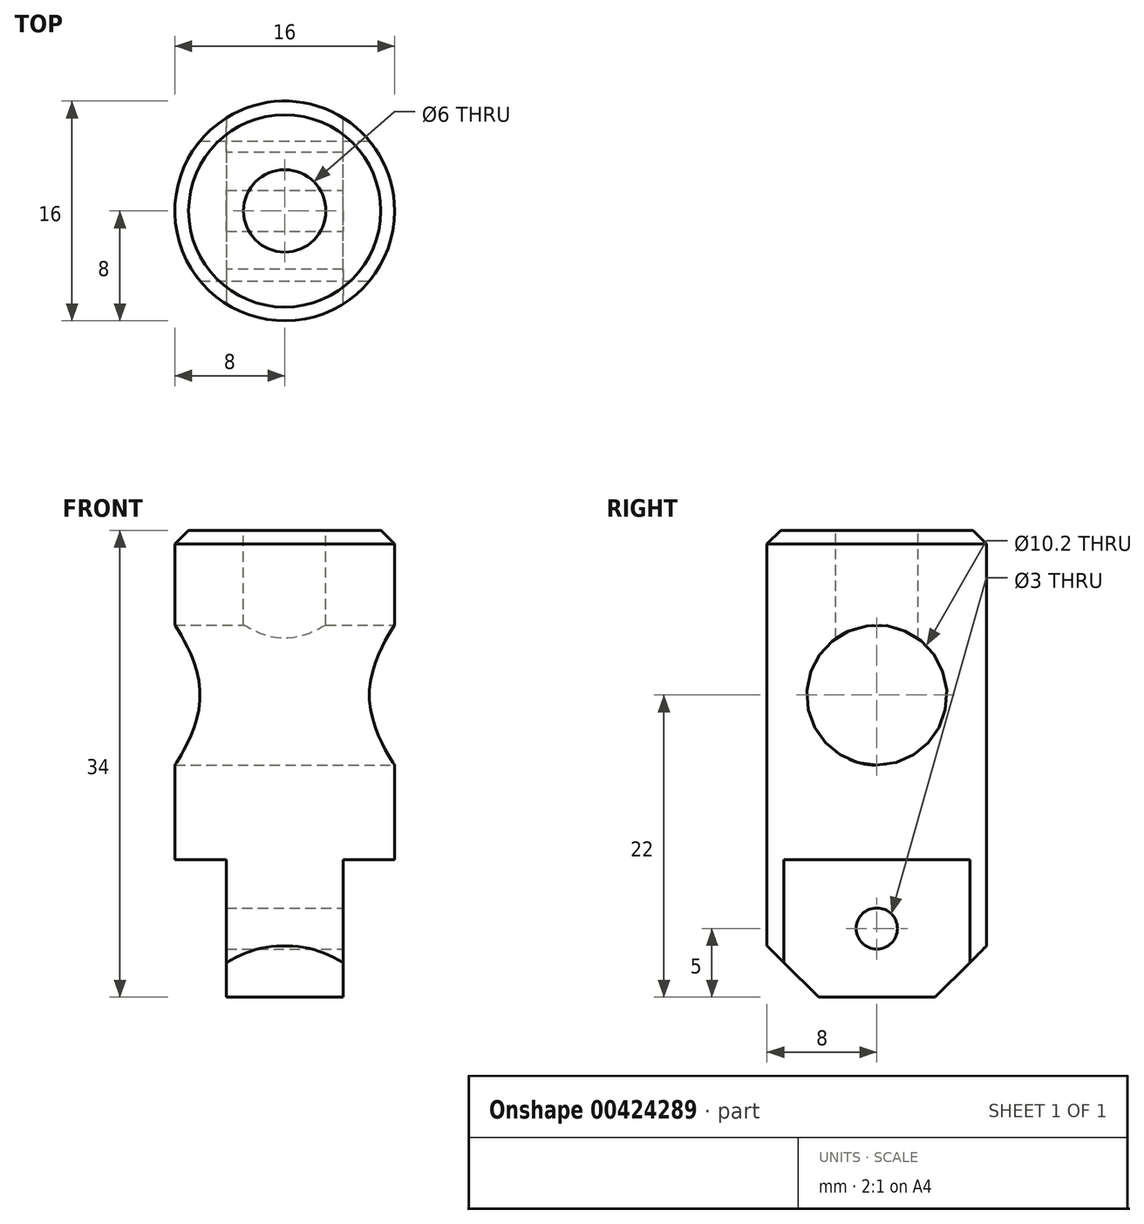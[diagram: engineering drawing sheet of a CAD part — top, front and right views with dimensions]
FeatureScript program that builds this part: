
annotation { "Feature Type Name" : "Feature", "Feature Type Description" : "" }
export const myFeature = defineFeature(function(context is Context, id is Id, definition is map)
    precondition{}
    {
        {
            var Q0;
            Q0=qCreatedBy(makeId("Top.planeOp"),FACE);
            var sketch = newSketch(context, id + "F0", { "sketchPlane" : qUnion([Q0])});
            skCircle(sketch, "E0", {"center": v(0, 0) * mm, "radius": 8 * mm});
            skSolve(sketch);
        }
        {
            var Q0;
            Q0 = qSketchRegion(id + "F0", true);
            extrude(context, id + "F1", {"entities" : qUnion([Q0]), "depth" : 34 * mm});
        }
        {
            var Q0;
            Q0=qCreatedBy(makeId("Right.planeOp"),FACE);
            var sketch = newSketch(context, id + "F2", { "sketchPlane" : qUnion([Q0])});
            skCircle(sketch, "E1", {"center": v(0, 22) * mm, "radius": 5.1 * mm});
            skCircle(sketch, "E2", {"center": v(0, 5) * mm, "radius": 1.5 * mm});
            skSolve(sketch);
        }
        {
            var Q0;
            Q0 = qSketchRegion(id + "F2", true);
            extrude(context, id + "F3", {"entities" : qUnion([Q0]), "operationType" : NewBodyOperationType.REMOVE, "endBound" : BoundingType.SYMMETRIC, "oppositeDirection" : true, "depth" : 100 * mm});
        }
        {
            var Q0;
            Q0=makeQuery(id+"F1.opExtrude","CAP_EDGE",EDGE,{"disambiguationData":[OSD([sQuery(id+"F0.wireOp",EDGE,"E0")])],"isStart":false});
            chamfer(context, id + "F4", {"entities" : qUnion([Q0]), "width" : 1 * mm, "tangentPropagation" : true});
        }
        {
            var Q0;
            Q0=qCreatedBy(makeId("Top.planeOp"),FACE);
            var sketch = newSketch(context, id + "F5", { "sketchPlane" : qUnion([Q0])});
            skLineSegment(sketch, "E3.bottom", {"start": v(13.33, 8.8) * mm, "end": v(4.25, 8.8) * mm});
            skLineSegment(sketch, "E3.top", {"start": v(13.33, -8.8) * mm, "end": v(4.25, -8.8) * mm});
            skLineSegment(sketch, "E3.left", {"start": v(13.33, 8.8) * mm, "end": v(13.33, -8.8) * mm});
            skLineSegment(sketch, "E3.right", {"start": v(-13.33, 8.8) * mm, "end": v(-13.33, -8.8) * mm});
            skPoint(sketch, "E3.middle", {"position": v(0, 0) * mm});
            skLineSegment(sketch, "E4", {"start": v(-4.25, 0) * mm, "end": v(-4.25, -8.8) * mm});
            skLineSegment(sketch, "E5", {"start": v(-4.25, -8.8) * mm, "end": v(-4.25, 8.8) * mm});
            skLineSegment(sketch, "E6", {"start": v(4.25, 0) * mm, "end": v(4.25, -8.8) * mm});
            skLineSegment(sketch, "E7", {"start": v(4.25, -8.8) * mm, "end": v(4.25, 8.8) * mm});
            skLineSegment(sketch, "E8.trimOffspring", {"start": v(-4.25, 8.8) * mm, "end": v(-13.33, 8.8) * mm});
            skLineSegment(sketch, "E9.trimOffspring", {"start": v(-4.25, -8.8) * mm, "end": v(-13.33, -8.8) * mm});
            skSolve(sketch);
        }
        {
            var Q0;
            Q0 = qSketchRegion(id + "F5", true);
            extrude(context, id + "F6", {"entities" : qUnion([Q0]), "operationType" : NewBodyOperationType.REMOVE, "depth" : 10 * mm});
        }
        {
            var Q0;
            Q0=makeQuery(id+"F6.boolean.opBoolean","COPY",FACE,{"derivedFrom":makeQuery(id+"F6.opExtrude","SWEPT_FACE",FACE,{"disambiguationData":[OSD([sQuery(id+"F5.wireOp",EDGE,"E5")])]})});
            var sketch = newSketch(context, id + "F7", { "sketchPlane" : qUnion([Q0])});
            skLineSegment(sketch, "E10", {"start": v(0, 0) * mm, "end": v(-4.25, 0) * mm});
            skLineSegment(sketch, "E11", {"start": v(-4.25, 0) * mm, "end": v(4.25, 0) * mm});
            skLineSegment(sketch, "E12", {"start": v(-4.25, 0) * mm, "end": v(-9.1, 4.85) * mm});
            skLineSegment(sketch, "E13", {"start": v(-4.25, 0) * mm, "end": v(-9.4, 0) * mm});
            skLineSegment(sketch, "E14", {"start": v(4.25, 0) * mm, "end": v(10.14, 0) * mm});
            skLineSegment(sketch, "E15", {"start": v(4.25, 0) * mm, "end": v(8.72, 4.47) * mm});
            skLineSegment(sketch, "E16", {"start": v(-9.1, 4.85) * mm, "end": v(-9.4, 0) * mm});
            skLineSegment(sketch, "E17", {"start": v(8.72, 4.47) * mm, "end": v(10.14, 0) * mm});
            skSolve(sketch);
        }
        {
            var Q0;
            Q0 = qSketchRegion(id + "F7", true);
            extrude(context, id + "F8", {"entities" : qUnion([Q0]), "operationType" : NewBodyOperationType.REMOVE, "oppositeDirection" : true, "depth" : 25 * mm});
        }
        {
            var Q0;
            Q0=qCreatedBy(makeId("Top.planeOp"),FACE);
            var sketch = newSketch(context, id + "F9", { "sketchPlane" : qUnion([Q0])});
            skCircle(sketch, "E18", {"center": v(0, 0) * mm, "radius": 3.3 * mm});
            skSolve(sketch);
        }
        {
            var Q0;
            Q0 = qSketchRegion(id + "F9", true);
            extrude(context, id + "F10", {"entities" : qUnion([Q0]), "operationType" : NewBodyOperationType.REMOVE, "oppositeDirection" : true, "depth" : 12 * mm});
        }
        {
            var Q0;
            Q0=makeQuery(id+"F1.opExtrude","CAP_FACE",FACE,{"disambiguationData":[OSD([sQuery(id+"F0.wireOp",EDGE,"E0")])],"isStart":false});
            var sketch = newSketch(context, id + "F11", { "sketchPlane" : qUnion([Q0])});
            skSolve(sketch);
        }
        {
            var Q0;
            {var subQ0=sQuery(id+"F0.wireOp",EDGE,"E0");Q0=makeQuery(id+"F11.imprint","IMPRINT",FACE,{"disambiguationData":[TD([[makeQuery(id+"F11.imprint","IMPRINT",EDGE,{"derivedFrom":makeQuery(id+"F4.opChamfer","BLEND_EDGE",EDGE,{"blendedFrom":[makeQuery(id+"F1.opExtrude","CAP_EDGE",EDGE,{"disambiguationData":[OSD([subQ0])],"isStart":false}),makeQuery(id+"F1.opExtrude","CAP_FACE",FACE,{"disambiguationData":[OSD([subQ0])],"isStart":false})],"blendedInto":[makeQuery(id+"F1.opExtrude","CAP_FACE",FACE,{"disambiguationData":[OSD([subQ0])],"isStart":false})]})}),1.0]])]});}
            var sketch = newSketch(context, id + "F12", { "sketchPlane" : qUnion([Q0])});
            skCircle(sketch, "E19", {"center": v(0, 0) * mm, "radius": 3 * mm});
            skSolve(sketch);
        }
        {
            var Q0;
            Q0 = qSketchRegion(id + "F12", true);
            extrude(context, id + "F13", {"entities" : qUnion([Q0]), "operationType" : NewBodyOperationType.REMOVE, "oppositeDirection" : true, "depth" : 12 * mm});
        }
    });
